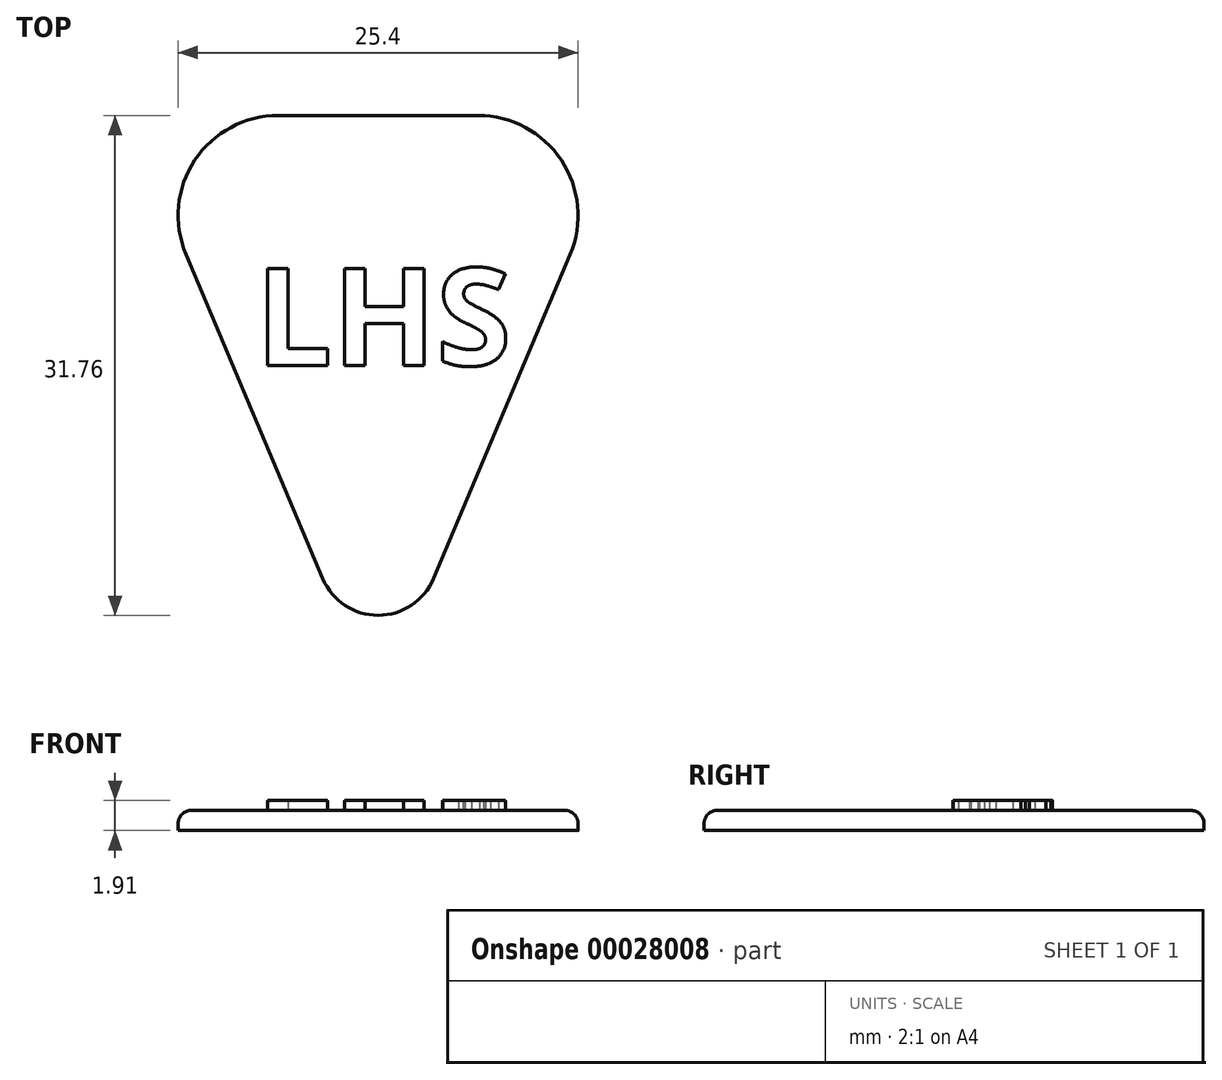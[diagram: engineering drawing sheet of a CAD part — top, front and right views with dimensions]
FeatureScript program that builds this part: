
annotation { "Feature Type Name" : "Feature", "Feature Type Description" : "" }
export const myFeature = defineFeature(function(context is Context, id is Id, definition is map)
    precondition{}
    {
        {
            var Q0;
            Q0=qCreatedBy(makeId("Top.planeOp"),FACE);
            var sketch = newSketch(context, id + "F0", { "sketchPlane" : qUnion([Q0])});
            skLineSegment(sketch, "E0.bottom", {"start": v(-12.7, 15.88) * mm, "end": v(12.7, 15.88) * mm, "construction": true});
            skLineSegment(sketch, "E0.top", {"start": v(-12.7, -15.88) * mm, "end": v(12.7, -15.88) * mm, "construction": true});
            skLineSegment(sketch, "E0.left", {"start": v(-12.7, 15.88) * mm, "end": v(-12.7, -15.88) * mm, "construction": true});
            skLineSegment(sketch, "E0.right", {"start": v(12.7, 15.88) * mm, "end": v(12.7, -15.88) * mm, "construction": true});
            skLineSegment(sketch, "E1", {"start": v(0, 15.88) * mm, "end": v(0, -15.88) * mm, "construction": true});
            skCircle(sketch, "E2", {"center": v(-6.35, 9.52) * mm, "radius": 6.35 * mm});
            skCircle(sketch, "E3", {"center": v(0, -12.07) * mm, "radius": 3.81 * mm});
            skCircle(sketch, "E4.MirrorC", {"center": v(6.35, 9.52) * mm, "radius": 6.35 * mm});
            skLineSegment(sketch, "E5", {"start": v(-6.35, 15.88) * mm, "end": v(6.35, 15.87) * mm});
            skLineSegment(sketch, "E6", {"start": v(-12.2, 7.06) * mm, "end": v(-3.51, -13.55) * mm});
            skLineSegment(sketch, "E7.MirrorCS", {"start": v(12.2, 7.06) * mm, "end": v(3.51, -13.55) * mm});
            skSolve(sketch);
        }
        {
            var Q0;
            Q0 = qSketchRegion(id + "F0", true);
            extrude(context, id + "F1", {"entities" : qUnion([Q0]), "depth" : 1.27 * mm});
        }
        {
            var Q0;
            Q0=makeQuery(id+"F1.opExtrude","CAP_EDGE",EDGE,{"disambiguationData":[OSD([sQuery(id+"F0.wireOp",EDGE,"E6")])],"isStart":false});
            fillet(context, id + "F2", {"entities" : qUnion([Q0]), "radius" : 0.83 * mm, "tangentPropagation" : true, "allowEdgeOverflow" : false});
        }
        {
            var Q0;
            Q0=makeQuery(id+"F1.opExtrude","CAP_FACE",FACE,{"disambiguationData":[OSD([sQuery(id+"F0.wireOp",EDGE,"E2"),sQuery(id+"F0.wireOp",EDGE,"E3"),sQuery(id+"F0.wireOp",EDGE,"E4.MirrorC"),sQuery(id+"F0.wireOp",EDGE,"E5"),sQuery(id+"F0.wireOp",EDGE,"E6"),sQuery(id+"F0.wireOp",EDGE,"E7.MirrorCS")])],"isStart":false});
            var sketch = newSketch(context, id + "F3", { "sketchPlane" : qUnion([Q0])});
            skLineSegment(sketch, "E8", {"start": v(-8.33, 0) * mm, "end": v(8.33, 0) * mm, "construction": true});
            skText(sketch, "E9", { "text": "LHS", "fontName": "OpenSans-Bold.ttf"});
            const initialGuessF3  = {"E9": [-0.0078, 0, 1, 0, 0.00622]};
            skSetInitialGuess(sketch, initialGuessF3);
            skSolve(sketch);
        }
        {
            var Q0;
            Q0 = qSketchRegion(id + "F3", true);
            extrude(context, id + "F4", {"entities" : qUnion([Q0]), "operationType" : NewBodyOperationType.ADD, "depth" : 0.64 * mm});
        }
    });
